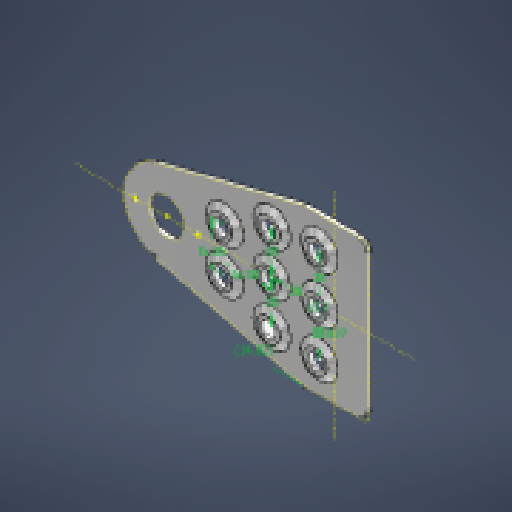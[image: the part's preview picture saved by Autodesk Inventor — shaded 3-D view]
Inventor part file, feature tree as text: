
AUTODESK INVENTOR PART (.ipt)
format: ipt  version: 2024.3 (Build 283343000, 343)  size: 325,632 bytes
history: native  units: mm (DEFAULTED — no unit token found)
features: sketch x5, sheet_metal_op x4, other x4, hole x3, chamfer x1, projected_geometry x1
ambient origin geometry x8: Origin, YZ Plane, XZ Plane, XY Plane, X Axis, Y Axis, Z Axis, Center Point
bodies: Solid1 (feature_tree)
feature tree (18):
  sheet_metal_op  "Face1"
  hole  "Hole1"  [1 undecoded]
  hole  "Hole2"  [1 undecoded]
  sketch  "Sketch6"  dims[d5=28.575mm d6=6.0mm d7=15.0mm d8=9.0mm d9=90.0deg d10=3.048mm d11=20.594885mm]
  hole  "Hole3"  [1 undecoded]
  sheet_metal_op  "Flange2"
  other  "Corner Chamfer1"
  chamfer  "Corner Round1"
  sketch  "Sketch2"  dims[d0=115.0mm d1=50.8mm]
  other  "Plate1"
  sketch  "Sketch3"  dims[d2=34.0mm d3=110.0mm]
  sketch  "Sketch4"  dims[d4=3.048mm]
  projected_geometry  "Projected Loop1"
  sketch  "Sketch7"  dims[d12=50.8mm d13=4.978mm d14=6.0mm d15=9.779mm d16=9.0mm d17=14.3117mm d18=8.0mm d19=20.594885mm d32=12.7mm d33=12.836856mm d49=2.041927mm d50=12.7mm d51=6.0mm d52=4.0mm d53=2.0mm d54=90.0deg d55=8.0mm d56=20.594885mm d78=20.0mm d80=38.0mm d81=10.0mm d83=10.0mm d85=20.0mm d87=38.0mm d88=10.0mm d90=10.0mm d92=20.0mm d94=38.0mm d95=10.0mm d97=10.0mm d99=20.0mm d101=35.0mm d102=10.0mm d104=10.0mm d106=20.0mm d108=35.0mm d109=10.0mm d111=10.0mm d114=38.0mm d115=35.0mm d117=0.0mm d118=3.048mm d119=1.524mm d120=6.096mm d121=4.572mm d122=20.0mm d123=90.0deg d124=1.0mm d125=12.192mm d126=3.048mm d127=4.572mm d128=14.0mm d129=6.0mm d130=45.0deg d131=8.0mm]
  other  "Plate3"
  sheet_metal_op  "Bend2"
  sheet_metal_op  "Corner2"
  other  "iFeature5:4"
note: 3 required parameter values undecoded (feature->parameter linkage not recoverable at this tier; creation-order binding heuristic only, values carry confidence <= 0.55)
